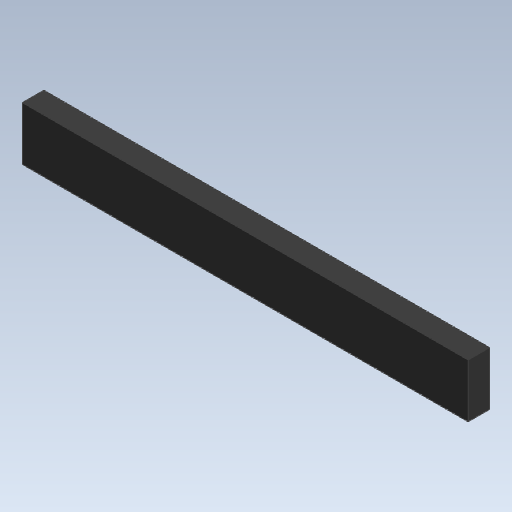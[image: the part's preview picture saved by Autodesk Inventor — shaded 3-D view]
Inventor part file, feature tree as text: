
AUTODESK INVENTOR PART (.ipt)
format: ipt  version: 2020 (Build 240168000, 168)  size: 84,992 bytes
history: native  units: mm
features: other x1, extrude x1
ambient origin geometry x8: Origin, YZ Plane, XZ Plane, XY Plane, X Axis, Y Axis, Z Axis, Center Point
bodies: Body1 (feature_tree)
feature tree (2):
  other  "實體1"
  extrude  "擠出1"  Depth=15.0mm
